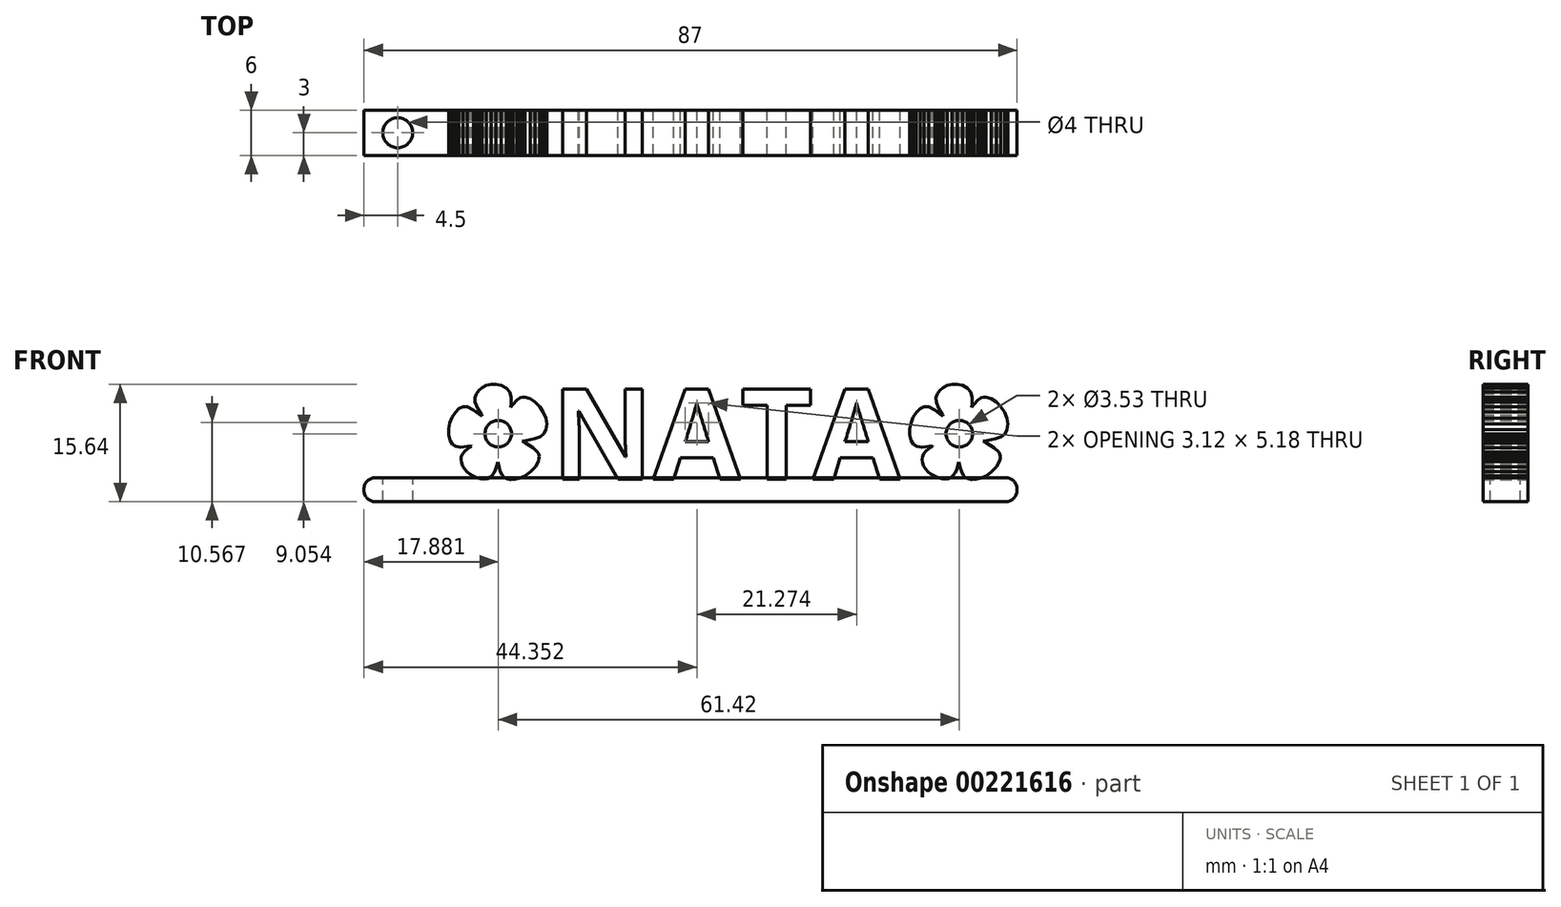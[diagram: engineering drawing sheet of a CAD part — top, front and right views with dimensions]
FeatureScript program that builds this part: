
annotation { "Feature Type Name" : "Feature", "Feature Type Description" : "" }
export const myFeature = defineFeature(function(context is Context, id is Id, definition is map)
    precondition{}
    {
        {
            var Q0;
            Q0=qCreatedBy(makeId("Front.planeOp"),FACE);
            var sketch = newSketch(context, id + "F0", { "sketchPlane" : qUnion([Q0])});
            skText(sketch, "E0", { "text": "    NATA", "fontName": "OpenSans-Bold.ttf"});
            skLineSegment(sketch, "E1.0.0", {"start": v(-9.3, 0.1) * mm, "end": v(-8.53, 0.46) * mm});
            skLineSegment(sketch, "E1.0.1", {"start": v(-8.53, 0.46) * mm, "end": v(-7.79, 1.02) * mm});
            skLineSegment(sketch, "E1.0.2", {"start": v(-7.79, 1.02) * mm, "end": v(-7.18, 1.67) * mm});
            skLineSegment(sketch, "E1.0.3", {"start": v(-7.18, 1.67) * mm, "end": v(-6.78, 2.35) * mm});
            skLineSegment(sketch, "E1.0.4", {"start": v(-6.78, 2.35) * mm, "end": v(-6.68, 2.7) * mm});
            skLineSegment(sketch, "E1.0.5", {"start": v(-6.68, 2.7) * mm, "end": v(-6.67, 3.02) * mm});
            skLineSegment(sketch, "E1.0.6", {"start": v(-6.67, 3.02) * mm, "end": v(-6.73, 3.33) * mm});
            skLineSegment(sketch, "E1.0.7", {"start": v(-6.73, 3.33) * mm, "end": v(-6.89, 3.62) * mm});
            skLineSegment(sketch, "E1.0.8", {"start": v(-6.89, 3.62) * mm, "end": v(-7.48, 4.2) * mm});
            skLineSegment(sketch, "E1.0.9", {"start": v(-7.48, 4.2) * mm, "end": v(-8.5, 4.79) * mm});
            skLineSegment(sketch, "E1.0.10", {"start": v(-8.5, 4.79) * mm, "end": v(-8.93, 5.06) * mm});
            skLineSegment(sketch, "E1.0.11", {"start": v(-8.93, 5.06) * mm, "end": v(-8.42, 5.16) * mm});
            skLineSegment(sketch, "E1.0.12", {"start": v(-8.42, 5.16) * mm, "end": v(-7.31, 5.37) * mm});
            skLineSegment(sketch, "E1.0.13", {"start": v(-7.31, 5.37) * mm, "end": v(-6.55, 5.65) * mm});
            skLineSegment(sketch, "E1.0.14", {"start": v(-6.55, 5.65) * mm, "end": v(-6.05, 6.04) * mm});
            skLineSegment(sketch, "E1.0.15", {"start": v(-6.05, 6.04) * mm, "end": v(-5.76, 6.58) * mm});
            skLineSegment(sketch, "E1.0.16", {"start": v(-5.76, 6.58) * mm, "end": v(-5.64, 7.33) * mm});
            skLineSegment(sketch, "E1.0.17", {"start": v(-5.64, 7.33) * mm, "end": v(-5.78, 8.14) * mm});
            skLineSegment(sketch, "E1.0.18", {"start": v(-5.78, 8.14) * mm, "end": v(-6.1, 8.93) * mm});
            skLineSegment(sketch, "E1.0.19", {"start": v(-6.1, 8.93) * mm, "end": v(-6.6, 9.67) * mm});
            skLineSegment(sketch, "E1.0.20", {"start": v(-6.6, 9.67) * mm, "end": v(-7.2, 10.28) * mm});
            skLineSegment(sketch, "E1.0.21", {"start": v(-7.2, 10.28) * mm, "end": v(-7.86, 10.72) * mm});
            skLineSegment(sketch, "E1.0.22", {"start": v(-7.86, 10.72) * mm, "end": v(-8.55, 10.93) * mm});
            skLineSegment(sketch, "E1.0.23", {"start": v(-8.55, 10.93) * mm, "end": v(-8.88, 10.93) * mm});
            skLineSegment(sketch, "E1.0.24", {"start": v(-8.88, 10.93) * mm, "end": v(-9.2, 10.85) * mm});
            skLineSegment(sketch, "E1.0.25", {"start": v(-9.2, 10.85) * mm, "end": v(-9.65, 10.56) * mm});
            skLineSegment(sketch, "E1.0.26", {"start": v(-9.65, 10.56) * mm, "end": v(-10.14, 9.98) * mm});
            skLineSegment(sketch, "E1.0.27", {"start": v(-10.14, 9.98) * mm, "end": v(-10.45, 9.58) * mm});
            skLineSegment(sketch, "E1.0.28", {"start": v(-10.45, 9.58) * mm, "end": v(-10.4, 10.03) * mm});
            skLineSegment(sketch, "E1.0.29", {"start": v(-10.4, 10.03) * mm, "end": v(-10.4, 10.93) * mm});
            skLineSegment(sketch, "E1.0.30", {"start": v(-10.4, 10.93) * mm, "end": v(-10.6, 11.63) * mm});
            skLineSegment(sketch, "E1.0.31", {"start": v(-10.6, 11.63) * mm, "end": v(-11.04, 12.15) * mm});
            skLineSegment(sketch, "E1.0.32", {"start": v(-11.04, 12.15) * mm, "end": v(-11.71, 12.5) * mm});
            skLineSegment(sketch, "E1.0.33", {"start": v(-11.71, 12.5) * mm, "end": v(-12.4, 12.64) * mm});
            skLineSegment(sketch, "E1.0.34", {"start": v(-12.4, 12.64) * mm, "end": v(-13.07, 12.62) * mm});
            skLineSegment(sketch, "E1.0.35", {"start": v(-13.07, 12.62) * mm, "end": v(-13.7, 12.47) * mm});
            skLineSegment(sketch, "E1.0.36", {"start": v(-13.7, 12.47) * mm, "end": v(-14.26, 12.2) * mm});
            skLineSegment(sketch, "E1.0.37", {"start": v(-14.26, 12.2) * mm, "end": v(-14.72, 11.83) * mm});
            skLineSegment(sketch, "E1.0.38", {"start": v(-14.72, 11.83) * mm, "end": v(-15.05, 11.38) * mm});
            skLineSegment(sketch, "E1.0.39", {"start": v(-15.05, 11.38) * mm, "end": v(-15.22, 10.87) * mm});
            skLineSegment(sketch, "E1.0.40", {"start": v(-15.22, 10.87) * mm, "end": v(-15.2, 10.3) * mm});
            skLineSegment(sketch, "E1.0.41", {"start": v(-15.2, 10.3) * mm, "end": v(-14.83, 9.4) * mm});
            skLineSegment(sketch, "E1.0.42", {"start": v(-14.83, 9.4) * mm, "end": v(-14.35, 8.55) * mm});
            skLineSegment(sketch, "E1.0.43", {"start": v(-14.35, 8.55) * mm, "end": v(-14.3, 8.4) * mm});
            skLineSegment(sketch, "E1.0.44", {"start": v(-14.3, 8.4) * mm, "end": v(-14.48, 8.53) * mm});
            skLineSegment(sketch, "E1.0.45", {"start": v(-14.48, 8.53) * mm, "end": v(-15.4, 9.23) * mm});
            skLineSegment(sketch, "E1.0.46", {"start": v(-15.4, 9.23) * mm, "end": v(-16.22, 9.63) * mm});
            skLineSegment(sketch, "E1.0.47", {"start": v(-16.22, 9.63) * mm, "end": v(-16.8, 9.63) * mm});
            skLineSegment(sketch, "E1.0.48", {"start": v(-16.8, 9.63) * mm, "end": v(-17.36, 9.37) * mm});
            skLineSegment(sketch, "E1.0.49", {"start": v(-17.36, 9.37) * mm, "end": v(-17.85, 8.9) * mm});
            skLineSegment(sketch, "E1.0.50", {"start": v(-17.85, 8.9) * mm, "end": v(-18.26, 8.26) * mm});
            skLineSegment(sketch, "E1.0.51", {"start": v(-18.26, 8.26) * mm, "end": v(-18.56, 7.51) * mm});
            skLineSegment(sketch, "E1.0.52", {"start": v(-18.56, 7.51) * mm, "end": v(-18.72, 6.71) * mm});
            skLineSegment(sketch, "E1.0.53", {"start": v(-18.72, 6.71) * mm, "end": v(-18.72, 5.9) * mm});
            skLineSegment(sketch, "E1.0.54", {"start": v(-18.72, 5.9) * mm, "end": v(-18.52, 5.16) * mm});
            skLineSegment(sketch, "E1.0.55", {"start": v(-18.52, 5.16) * mm, "end": v(-18.2, 4.64) * mm});
            skLineSegment(sketch, "E1.0.56", {"start": v(-18.2, 4.64) * mm, "end": v(-17.75, 4.36) * mm});
            skLineSegment(sketch, "E1.0.57", {"start": v(-17.75, 4.36) * mm, "end": v(-17.1, 4.27) * mm});
            skLineSegment(sketch, "E1.0.58", {"start": v(-17.1, 4.27) * mm, "end": v(-16.21, 4.37) * mm});
            skLineSegment(sketch, "E1.0.59", {"start": v(-16.21, 4.37) * mm, "end": v(-15.7, 4.43) * mm});
            skLineSegment(sketch, "E1.0.60", {"start": v(-15.7, 4.43) * mm, "end": v(-15.67, 4.4) * mm});
            skLineSegment(sketch, "E1.0.61", {"start": v(-15.67, 4.4) * mm, "end": v(-15.78, 4.33) * mm});
            skLineSegment(sketch, "E1.0.62", {"start": v(-15.78, 4.33) * mm, "end": v(-16.17, 4.07) * mm});
            skLineSegment(sketch, "E1.0.63", {"start": v(-16.17, 4.07) * mm, "end": v(-16.55, 3.71) * mm});
            skLineSegment(sketch, "E1.0.64", {"start": v(-16.55, 3.71) * mm, "end": v(-16.87, 3.33) * mm});
            skLineSegment(sketch, "E1.0.65", {"start": v(-16.87, 3.33) * mm, "end": v(-17.04, 3) * mm});
            skLineSegment(sketch, "E1.0.66", {"start": v(-17.04, 3) * mm, "end": v(-17.08, 2.6) * mm});
            skLineSegment(sketch, "E1.0.67", {"start": v(-17.08, 2.6) * mm, "end": v(-17.02, 2.2) * mm});
            skLineSegment(sketch, "E1.0.68", {"start": v(-17.02, 2.2) * mm, "end": v(-16.87, 1.78) * mm});
            skLineSegment(sketch, "E1.0.69", {"start": v(-16.87, 1.78) * mm, "end": v(-16.62, 1.39) * mm});
            skLineSegment(sketch, "E1.0.70", {"start": v(-16.62, 1.39) * mm, "end": v(-16.3, 1.02) * mm});
            skLineSegment(sketch, "E1.0.71", {"start": v(-16.3, 1.02) * mm, "end": v(-15.9, 0.69) * mm});
            skLineSegment(sketch, "E1.0.72", {"start": v(-15.9, 0.69) * mm, "end": v(-15.45, 0.4) * mm});
            skLineSegment(sketch, "E1.0.73", {"start": v(-15.45, 0.4) * mm, "end": v(-14.95, 0.2) * mm});
            skLineSegment(sketch, "E1.0.74", {"start": v(-14.95, 0.2) * mm, "end": v(-14.44, 0.06) * mm});
            skLineSegment(sketch, "E1.0.75", {"start": v(-14.44, 0.06) * mm, "end": v(-13.98, 0.02) * mm});
            skLineSegment(sketch, "E1.0.76", {"start": v(-13.98, 0.02) * mm, "end": v(-13.58, 0.08) * mm});
            skLineSegment(sketch, "E1.0.77", {"start": v(-13.58, 0.08) * mm, "end": v(-13.23, 0.23) * mm});
            skLineSegment(sketch, "E1.0.78", {"start": v(-13.23, 0.23) * mm, "end": v(-12.92, 0.49) * mm});
            skLineSegment(sketch, "E1.0.79", {"start": v(-12.92, 0.49) * mm, "end": v(-12.67, 0.84) * mm});
            skLineSegment(sketch, "E1.0.80", {"start": v(-12.67, 0.84) * mm, "end": v(-12.46, 1.28) * mm});
            skLineSegment(sketch, "E1.0.81", {"start": v(-12.46, 1.28) * mm, "end": v(-12.3, 1.83) * mm});
            skLineSegment(sketch, "E1.0.82", {"start": v(-12.3, 1.83) * mm, "end": v(-12.19, 2.26) * mm});
            skLineSegment(sketch, "E1.0.83", {"start": v(-12.19, 2.26) * mm, "end": v(-12.13, 2.1) * mm});
            skLineSegment(sketch, "E1.0.84", {"start": v(-12.13, 2.1) * mm, "end": v(-12.01, 1.53) * mm});
            skLineSegment(sketch, "E1.0.85", {"start": v(-12.01, 1.53) * mm, "end": v(-11.82, 1) * mm});
            skLineSegment(sketch, "E1.0.86", {"start": v(-11.82, 1) * mm, "end": v(-11.6, 0.55) * mm});
            skLineSegment(sketch, "E1.0.87", {"start": v(-11.6, 0.55) * mm, "end": v(-11.35, 0.26) * mm});
            skLineSegment(sketch, "E1.0.88", {"start": v(-11.35, 0.26) * mm, "end": v(-10.95, 0.05) * mm});
            skLineSegment(sketch, "E1.0.89", {"start": v(-10.95, 0.05) * mm, "end": v(-10.46, -0.04) * mm});
            skLineSegment(sketch, "E1.0.90", {"start": v(-10.46, -0.04) * mm, "end": v(-9.9, -0.03) * mm});
            skLineSegment(sketch, "E1.0.91", {"start": v(-9.9, -0.03) * mm, "end": v(-9.3, 0.1) * mm});
            skCircle(sketch, "E2", {"center": v(-12.12, 6.05) * mm, "radius": 1.77 * mm});
            skCircle(sketch, "E3.1.0.0", {"center": v(49.3, 6.05) * mm, "radius": 1.77 * mm});
            skLineSegment(sketch, "E3.1.0.1", {"start": v(50.97, 9.58) * mm, "end": v(51.01, 10.03) * mm});
            skLineSegment(sketch, "E3.1.0.2", {"start": v(54.22, 10.28) * mm, "end": v(53.56, 10.72) * mm});
            skLineSegment(sketch, "E3.1.0.3", {"start": v(42.7, 5.9) * mm, "end": v(42.9, 5.16) * mm});
            skLineSegment(sketch, "E3.1.0.4", {"start": v(47.16, 12.2) * mm, "end": v(46.7, 11.83) * mm});
            skLineSegment(sketch, "E3.1.0.5", {"start": v(45.12, 1.02) * mm, "end": v(45.51, 0.69) * mm});
            skLineSegment(sketch, "E3.1.0.6", {"start": v(45.2, 9.63) * mm, "end": v(44.62, 9.63) * mm});
            skLineSegment(sketch, "E3.1.0.7", {"start": v(42.86, 7.51) * mm, "end": v(42.7, 6.71) * mm});
            skLineSegment(sketch, "E3.1.0.8", {"start": v(46.03, 9.23) * mm, "end": v(45.2, 9.63) * mm});
            skLineSegment(sketch, "E3.1.0.9", {"start": v(44.62, 9.63) * mm, "end": v(44.06, 9.37) * mm});
            skLineSegment(sketch, "E3.1.0.10", {"start": v(51.28, 9.98) * mm, "end": v(50.97, 9.58) * mm});
            skLineSegment(sketch, "E3.1.0.11", {"start": v(50.82, 11.63) * mm, "end": v(50.38, 12.15) * mm});
            skLineSegment(sketch, "E3.1.0.12", {"start": v(50.38, 12.15) * mm, "end": v(49.7, 12.5) * mm});
            skLineSegment(sketch, "E3.1.0.13", {"start": v(51.03, 10.93) * mm, "end": v(50.82, 11.63) * mm});
            skLineSegment(sketch, "E3.1.0.14", {"start": v(45.97, 0.4) * mm, "end": v(46.47, 0.2) * mm});
            skLineSegment(sketch, "E3.1.0.15", {"start": v(51.52, -0.03) * mm, "end": v(52.11, 0.1) * mm});
            skLineSegment(sketch, "E3.1.0.16", {"start": v(42.7, 6.71) * mm, "end": v(42.7, 5.9) * mm});
            skLineSegment(sketch, "E3.1.0.17", {"start": v(52.11, 0.1) * mm, "end": v(52.89, 0.46) * mm});
            skLineSegment(sketch, "E3.1.0.18", {"start": v(45.51, 0.69) * mm, "end": v(45.97, 0.4) * mm});
            skLineSegment(sketch, "E3.1.0.19", {"start": v(42.9, 5.16) * mm, "end": v(43.22, 4.64) * mm});
            skLineSegment(sketch, "E3.1.0.20", {"start": v(54.1, 5.37) * mm, "end": v(54.87, 5.65) * mm});
            skLineSegment(sketch, "E3.1.0.21", {"start": v(52.89, 0.46) * mm, "end": v(53.63, 1.02) * mm});
            skLineSegment(sketch, "E3.1.0.22", {"start": v(54.82, 9.67) * mm, "end": v(54.22, 10.28) * mm});
            skLineSegment(sketch, "E3.1.0.23", {"start": v(51.01, 10.03) * mm, "end": v(51.03, 10.93) * mm});
            skLineSegment(sketch, "E3.1.0.24", {"start": v(44.06, 9.37) * mm, "end": v(43.57, 8.9) * mm});
            skLineSegment(sketch, "E3.1.0.25", {"start": v(49.7, 12.5) * mm, "end": v(49.02, 12.64) * mm});
            skLineSegment(sketch, "E3.1.0.26", {"start": v(48.35, 12.62) * mm, "end": v(47.72, 12.47) * mm});
            skLineSegment(sketch, "E3.1.0.27", {"start": v(54.24, 1.67) * mm, "end": v(54.64, 2.35) * mm});
            skLineSegment(sketch, "E3.1.0.28", {"start": v(55.31, 8.93) * mm, "end": v(54.82, 9.67) * mm});
            skLineSegment(sketch, "E3.1.0.29", {"start": v(49.02, 12.64) * mm, "end": v(48.35, 12.62) * mm});
            skLineSegment(sketch, "E3.1.0.30", {"start": v(53.63, 1.02) * mm, "end": v(54.24, 1.67) * mm});
            skLineSegment(sketch, "E3.1.0.31", {"start": v(43.57, 8.9) * mm, "end": v(43.16, 8.26) * mm});
            skLineSegment(sketch, "E3.1.0.32", {"start": v(43.16, 8.26) * mm, "end": v(42.86, 7.51) * mm});
            skLineSegment(sketch, "E3.1.0.33", {"start": v(47.72, 12.47) * mm, "end": v(47.16, 12.2) * mm});
            skLineSegment(sketch, "E3.1.0.34", {"start": v(54.64, 2.35) * mm, "end": v(54.74, 2.7) * mm});
            skLineSegment(sketch, "E3.1.0.35", {"start": v(44.62, 9.63) * mm, "end": v(44.06, 9.37) * mm});
            skLineSegment(sketch, "E3.1.0.36", {"start": v(49.02, 12.64) * mm, "end": v(48.35, 12.62) * mm});
            skLineSegment(sketch, "E3.1.0.37", {"start": v(54.1, 5.37) * mm, "end": v(54.87, 5.65) * mm});
            skLineSegment(sketch, "E3.1.0.38", {"start": v(50.47, 0.05) * mm, "end": v(50.97, -0.04) * mm});
            skLineSegment(sketch, "E3.1.0.39", {"start": v(55.31, 8.93) * mm, "end": v(54.82, 9.67) * mm});
            skLineSegment(sketch, "E3.1.0.40", {"start": v(51.52, -0.03) * mm, "end": v(52.11, 0.1) * mm});
            skLineSegment(sketch, "E3.1.0.41", {"start": v(51.28, 9.98) * mm, "end": v(50.97, 9.58) * mm});
            skLineSegment(sketch, "E3.1.0.42", {"start": v(53.63, 1.02) * mm, "end": v(54.24, 1.67) * mm});
            skLineSegment(sketch, "E3.1.0.43", {"start": v(54.64, 2.35) * mm, "end": v(54.74, 2.7) * mm});
            skLineSegment(sketch, "E3.1.0.44", {"start": v(42.7, 6.71) * mm, "end": v(42.7, 5.9) * mm});
            skLineSegment(sketch, "E3.1.0.45", {"start": v(52.11, 0.1) * mm, "end": v(52.89, 0.46) * mm});
            skLineSegment(sketch, "E3.1.0.46", {"start": v(48.35, 12.62) * mm, "end": v(47.72, 12.47) * mm});
            skLineSegment(sketch, "E3.1.0.47", {"start": v(47.16, 12.2) * mm, "end": v(46.7, 11.83) * mm});
            skLineSegment(sketch, "E3.1.0.48", {"start": v(45.97, 0.4) * mm, "end": v(46.47, 0.2) * mm});
            skLineSegment(sketch, "E3.1.0.49", {"start": v(51.01, 10.03) * mm, "end": v(51.03, 10.93) * mm});
            skLineSegment(sketch, "E3.1.0.50", {"start": v(50.97, 9.58) * mm, "end": v(51.01, 10.03) * mm});
            skLineSegment(sketch, "E3.1.0.51", {"start": v(50.97, -0.04) * mm, "end": v(51.52, -0.03) * mm});
            skLineSegment(sketch, "E3.1.0.52", {"start": v(45.2, 9.63) * mm, "end": v(44.62, 9.63) * mm});
            skLineSegment(sketch, "E3.1.0.53", {"start": v(51.03, 10.93) * mm, "end": v(50.82, 11.63) * mm});
            skLineSegment(sketch, "E3.1.0.54", {"start": v(54.22, 10.28) * mm, "end": v(53.56, 10.72) * mm});
            skLineSegment(sketch, "E3.1.0.55", {"start": v(43.57, 8.9) * mm, "end": v(43.16, 8.26) * mm});
            skLineSegment(sketch, "E3.1.0.56", {"start": v(45.51, 0.69) * mm, "end": v(45.97, 0.4) * mm});
            skLineSegment(sketch, "E3.1.0.57", {"start": v(49.7, 12.5) * mm, "end": v(49.02, 12.64) * mm});
            skLineSegment(sketch, "E3.1.0.58", {"start": v(44.06, 9.37) * mm, "end": v(43.57, 8.9) * mm});
            skLineSegment(sketch, "E3.1.0.59", {"start": v(42.7, 5.9) * mm, "end": v(42.9, 5.16) * mm});
            skLineSegment(sketch, "E3.1.0.60", {"start": v(50.38, 12.15) * mm, "end": v(49.7, 12.5) * mm});
            skLineSegment(sketch, "E3.1.0.61", {"start": v(46.03, 9.23) * mm, "end": v(45.2, 9.63) * mm});
            skLineSegment(sketch, "E3.1.0.62", {"start": v(52.89, 0.46) * mm, "end": v(53.63, 1.02) * mm});
            skLineSegment(sketch, "E3.1.0.63", {"start": v(50.82, 11.63) * mm, "end": v(50.38, 12.15) * mm});
            skLineSegment(sketch, "E3.1.0.64", {"start": v(43.16, 8.26) * mm, "end": v(42.86, 7.51) * mm});
            skLineSegment(sketch, "E3.1.0.65", {"start": v(54.24, 1.67) * mm, "end": v(54.64, 2.35) * mm});
            skLineSegment(sketch, "E3.1.0.66", {"start": v(42.86, 7.51) * mm, "end": v(42.7, 6.71) * mm});
            skLineSegment(sketch, "E3.1.0.67", {"start": v(45.12, 1.02) * mm, "end": v(45.51, 0.69) * mm});
            skLineSegment(sketch, "E3.1.0.68", {"start": v(42.9, 5.16) * mm, "end": v(43.22, 4.64) * mm});
            skLineSegment(sketch, "E3.1.0.69", {"start": v(47.72, 12.47) * mm, "end": v(47.16, 12.2) * mm});
            skLineSegment(sketch, "E3.1.0.70", {"start": v(54.82, 9.67) * mm, "end": v(54.22, 10.28) * mm});
            skLineSegment(sketch, "E3.1.0.71", {"start": v(46.7, 11.83) * mm, "end": v(46.37, 11.38) * mm});
            skLineSegment(sketch, "E3.1.0.72", {"start": v(53.56, 10.72) * mm, "end": v(52.87, 10.93) * mm});
            skLineSegment(sketch, "E3.1.0.73", {"start": v(55.37, 6.04) * mm, "end": v(55.67, 6.58) * mm});
            skLineSegment(sketch, "E3.1.0.74", {"start": v(54.74, 2.7) * mm, "end": v(54.76, 3.02) * mm});
            skLineSegment(sketch, "E3.1.0.75", {"start": v(52.87, 10.93) * mm, "end": v(52.54, 10.93) * mm});
            skLineSegment(sketch, "E3.1.0.76", {"start": v(43.22, 4.64) * mm, "end": v(43.67, 4.36) * mm});
            skLineSegment(sketch, "E3.1.0.77", {"start": v(52.22, 10.85) * mm, "end": v(51.77, 10.56) * mm});
            skLineSegment(sketch, "E3.1.0.78", {"start": v(53, 5.16) * mm, "end": v(54.1, 5.37) * mm});
            skLineSegment(sketch, "E3.1.0.79", {"start": v(54.76, 3.02) * mm, "end": v(54.69, 3.33) * mm});
            skLineSegment(sketch, "E3.1.0.80", {"start": v(54.69, 3.33) * mm, "end": v(54.53, 3.62) * mm});
            skLineSegment(sketch, "E3.1.0.81", {"start": v(53.94, 4.2) * mm, "end": v(52.93, 4.79) * mm});
            skLineSegment(sketch, "E3.1.0.82", {"start": v(55.78, 7.33) * mm, "end": v(55.65, 8.14) * mm});
            skLineSegment(sketch, "E3.1.0.83", {"start": v(44.8, 1.39) * mm, "end": v(45.12, 1.02) * mm});
            skLineSegment(sketch, "E3.1.0.84", {"start": v(46.98, 0.06) * mm, "end": v(47.44, 0.02) * mm});
            skLineSegment(sketch, "E3.1.0.85", {"start": v(52.5, 5.06) * mm, "end": v(53, 5.16) * mm});
            skLineSegment(sketch, "E3.1.0.86", {"start": v(50.07, 0.26) * mm, "end": v(50.47, 0.05) * mm});
            skLineSegment(sketch, "E3.1.0.87", {"start": v(46.37, 11.38) * mm, "end": v(46.2, 10.87) * mm});
            skLineSegment(sketch, "E3.1.0.88", {"start": v(55.67, 6.58) * mm, "end": v(55.78, 7.33) * mm});
            skLineSegment(sketch, "E3.1.0.89", {"start": v(50.47, 0.05) * mm, "end": v(50.97, -0.04) * mm});
            skLineSegment(sketch, "E3.1.0.90", {"start": v(52.93, 4.79) * mm, "end": v(52.5, 5.06) * mm});
            skLineSegment(sketch, "E3.1.0.91", {"start": v(46.47, 0.2) * mm, "end": v(46.98, 0.06) * mm});
            skLineSegment(sketch, "E3.1.0.92", {"start": v(46.22, 10.3) * mm, "end": v(46.6, 9.4) * mm});
            skLineSegment(sketch, "E3.1.0.93", {"start": v(44.55, 1.78) * mm, "end": v(44.8, 1.39) * mm});
            skLineSegment(sketch, "E3.1.0.94", {"start": v(54.53, 3.62) * mm, "end": v(53.94, 4.2) * mm});
            skLineSegment(sketch, "E3.1.0.95", {"start": v(50.97, -0.04) * mm, "end": v(51.52, -0.03) * mm});
            skLineSegment(sketch, "E3.1.0.96", {"start": v(46.2, 10.87) * mm, "end": v(46.22, 10.3) * mm});
            skLineSegment(sketch, "E3.1.0.97", {"start": v(54.87, 5.65) * mm, "end": v(55.37, 6.04) * mm});
            skLineSegment(sketch, "E3.1.0.98", {"start": v(52.54, 10.93) * mm, "end": v(52.22, 10.85) * mm});
            skLineSegment(sketch, "E3.1.0.99", {"start": v(51.77, 10.56) * mm, "end": v(51.28, 9.98) * mm});
            skLineSegment(sketch, "E3.1.0.100", {"start": v(47.44, 0.02) * mm, "end": v(47.84, 0.08) * mm});
            skLineSegment(sketch, "E3.1.0.101", {"start": v(44.4, 2.2) * mm, "end": v(44.55, 1.78) * mm});
            skLineSegment(sketch, "E3.1.0.102", {"start": v(55.65, 8.14) * mm, "end": v(55.31, 8.93) * mm});
            skLineSegment(sketch, "E3.1.0.103", {"start": v(52.93, 4.79) * mm, "end": v(52.5, 5.06) * mm});
            skLineSegment(sketch, "E3.1.0.104", {"start": v(52.5, 5.06) * mm, "end": v(53, 5.16) * mm});
            skLineSegment(sketch, "E3.1.0.105", {"start": v(43.22, 4.64) * mm, "end": v(43.67, 4.36) * mm});
            skLineSegment(sketch, "E3.1.0.106", {"start": v(49.82, 0.55) * mm, "end": v(50.07, 0.26) * mm});
            skLineSegment(sketch, "E3.1.0.107", {"start": v(50.07, 0.26) * mm, "end": v(50.47, 0.05) * mm});
            skLineSegment(sketch, "E3.1.0.108", {"start": v(44.55, 1.78) * mm, "end": v(44.8, 1.39) * mm});
            skLineSegment(sketch, "E3.1.0.109", {"start": v(54.53, 3.62) * mm, "end": v(53.94, 4.2) * mm});
            skLineSegment(sketch, "E3.1.0.110", {"start": v(53, 5.16) * mm, "end": v(54.1, 5.37) * mm});
            skLineSegment(sketch, "E3.1.0.111", {"start": v(46.22, 10.3) * mm, "end": v(46.6, 9.4) * mm});
            skLineSegment(sketch, "E3.1.0.112", {"start": v(54.87, 5.65) * mm, "end": v(55.37, 6.04) * mm});
            skLineSegment(sketch, "E3.1.0.113", {"start": v(51.77, 10.56) * mm, "end": v(51.28, 9.98) * mm});
            skLineSegment(sketch, "E3.1.0.114", {"start": v(55.67, 6.58) * mm, "end": v(55.78, 7.33) * mm});
            skLineSegment(sketch, "E3.1.0.115", {"start": v(46.2, 10.87) * mm, "end": v(46.22, 10.3) * mm});
            skLineSegment(sketch, "E3.1.0.116", {"start": v(52.54, 10.93) * mm, "end": v(52.22, 10.85) * mm});
            skLineSegment(sketch, "E3.1.0.117", {"start": v(47.44, 0.02) * mm, "end": v(47.84, 0.08) * mm});
            skLineSegment(sketch, "E3.1.0.118", {"start": v(52.22, 10.85) * mm, "end": v(51.77, 10.56) * mm});
            skLineSegment(sketch, "E3.1.0.119", {"start": v(46.98, 0.06) * mm, "end": v(47.44, 0.02) * mm});
            skLineSegment(sketch, "E3.1.0.120", {"start": v(46.47, 0.2) * mm, "end": v(46.98, 0.06) * mm});
            skLineSegment(sketch, "E3.1.0.121", {"start": v(53.94, 4.2) * mm, "end": v(52.93, 4.79) * mm});
            skLineSegment(sketch, "E3.1.0.122", {"start": v(55.37, 6.04) * mm, "end": v(55.67, 6.58) * mm});
            skLineSegment(sketch, "E3.1.0.123", {"start": v(44.34, 2.6) * mm, "end": v(44.4, 2.2) * mm});
            skLineSegment(sketch, "E3.1.0.124", {"start": v(54.74, 2.7) * mm, "end": v(54.76, 3.02) * mm});
            skLineSegment(sketch, "E3.1.0.125", {"start": v(44.8, 1.39) * mm, "end": v(45.12, 1.02) * mm});
            skLineSegment(sketch, "E3.1.0.126", {"start": v(55.65, 8.14) * mm, "end": v(55.31, 8.93) * mm});
            skLineSegment(sketch, "E3.1.0.127", {"start": v(55.78, 7.33) * mm, "end": v(55.65, 8.14) * mm});
            skLineSegment(sketch, "E3.1.0.128", {"start": v(54.76, 3.02) * mm, "end": v(54.69, 3.33) * mm});
            skLineSegment(sketch, "E3.1.0.129", {"start": v(44.4, 2.2) * mm, "end": v(44.55, 1.78) * mm});
            skLineSegment(sketch, "E3.1.0.130", {"start": v(54.69, 3.33) * mm, "end": v(54.53, 3.62) * mm});
            skLineSegment(sketch, "E3.1.0.131", {"start": v(46.37, 11.38) * mm, "end": v(46.2, 10.87) * mm});
            skLineSegment(sketch, "E3.1.0.132", {"start": v(52.87, 10.93) * mm, "end": v(52.54, 10.93) * mm});
            skLineSegment(sketch, "E3.1.0.133", {"start": v(53.56, 10.72) * mm, "end": v(52.87, 10.93) * mm});
            skLineSegment(sketch, "E3.1.0.134", {"start": v(46.7, 11.83) * mm, "end": v(46.37, 11.38) * mm});
            skLineSegment(sketch, "E3.1.0.135", {"start": v(44.34, 2.6) * mm, "end": v(44.4, 2.2) * mm});
            skLineSegment(sketch, "E3.1.0.136", {"start": v(45.2, 4.37) * mm, "end": v(45.72, 4.43) * mm});
            skLineSegment(sketch, "E3.1.0.137", {"start": v(49.4, 1.53) * mm, "end": v(49.6, 1) * mm});
            skLineSegment(sketch, "E3.1.0.138", {"start": v(45.64, 4.33) * mm, "end": v(45.26, 4.07) * mm});
            skLineSegment(sketch, "E3.1.0.139", {"start": v(48.2, 0.23) * mm, "end": v(48.5, 0.49) * mm});
            skLineSegment(sketch, "E3.1.0.140", {"start": v(48.75, 0.84) * mm, "end": v(48.96, 1.28) * mm});
            skLineSegment(sketch, "E3.1.0.141", {"start": v(49.6, 1) * mm, "end": v(49.82, 0.55) * mm});
            skLineSegment(sketch, "E3.1.0.142", {"start": v(45.26, 4.07) * mm, "end": v(44.87, 3.71) * mm});
            skLineSegment(sketch, "E3.1.0.143", {"start": v(49.29, 2.1) * mm, "end": v(49.4, 1.53) * mm});
            skLineSegment(sketch, "E3.1.0.144", {"start": v(48.5, 0.49) * mm, "end": v(48.75, 0.84) * mm});
            skLineSegment(sketch, "E3.1.0.145", {"start": v(44.31, 4.27) * mm, "end": v(45.2, 4.37) * mm});
            skLineSegment(sketch, "E3.1.0.146", {"start": v(44.87, 3.71) * mm, "end": v(44.55, 3.33) * mm});
            skLineSegment(sketch, "E3.1.0.147", {"start": v(43.67, 4.36) * mm, "end": v(44.31, 4.27) * mm});
            skLineSegment(sketch, "E3.1.0.148", {"start": v(48.96, 1.28) * mm, "end": v(49.12, 1.83) * mm});
            skLineSegment(sketch, "E3.1.0.149", {"start": v(49.23, 2.26) * mm, "end": v(49.29, 2.1) * mm});
            skLineSegment(sketch, "E3.1.0.150", {"start": v(44.55, 3.33) * mm, "end": v(44.38, 3) * mm});
            skLineSegment(sketch, "E3.1.0.151", {"start": v(49.82, 0.55) * mm, "end": v(50.07, 0.26) * mm});
            skLineSegment(sketch, "E3.1.0.152", {"start": v(49.12, 1.83) * mm, "end": v(49.23, 2.26) * mm});
            skLineSegment(sketch, "E3.1.0.153", {"start": v(44.38, 3) * mm, "end": v(44.34, 2.6) * mm});
            skLineSegment(sketch, "E3.1.0.154", {"start": v(47.84, 0.08) * mm, "end": v(48.2, 0.23) * mm});
            skLineSegment(sketch, "E3.1.0.155", {"start": v(45.75, 4.4) * mm, "end": v(45.64, 4.33) * mm});
            skLineSegment(sketch, "E3.1.0.156", {"start": v(49.23, 2.26) * mm, "end": v(49.29, 2.1) * mm});
            skLineSegment(sketch, "E3.1.0.157", {"start": v(44.31, 4.27) * mm, "end": v(45.2, 4.37) * mm});
            skLineSegment(sketch, "E3.1.0.158", {"start": v(49.4, 1.53) * mm, "end": v(49.6, 1) * mm});
            skLineSegment(sketch, "E3.1.0.159", {"start": v(45.72, 4.43) * mm, "end": v(45.75, 4.4) * mm});
            skLineSegment(sketch, "E3.1.0.160", {"start": v(44.87, 3.71) * mm, "end": v(44.55, 3.33) * mm});
            skLineSegment(sketch, "E3.1.0.161", {"start": v(43.67, 4.36) * mm, "end": v(44.31, 4.27) * mm});
            skLineSegment(sketch, "E3.1.0.162", {"start": v(45.2, 4.37) * mm, "end": v(45.72, 4.43) * mm});
            skLineSegment(sketch, "E3.1.0.163", {"start": v(47.84, 0.08) * mm, "end": v(48.2, 0.23) * mm});
            skLineSegment(sketch, "E3.1.0.164", {"start": v(45.26, 4.07) * mm, "end": v(44.87, 3.71) * mm});
            skLineSegment(sketch, "E3.1.0.165", {"start": v(49.29, 2.1) * mm, "end": v(49.4, 1.53) * mm});
            skLineSegment(sketch, "E3.1.0.166", {"start": v(49.12, 1.83) * mm, "end": v(49.23, 2.26) * mm});
            skLineSegment(sketch, "E3.1.0.167", {"start": v(45.64, 4.33) * mm, "end": v(45.26, 4.07) * mm});
            skLineSegment(sketch, "E3.1.0.168", {"start": v(48.2, 0.23) * mm, "end": v(48.5, 0.49) * mm});
            skLineSegment(sketch, "E3.1.0.169", {"start": v(44.38, 3) * mm, "end": v(44.34, 2.6) * mm});
            skLineSegment(sketch, "E3.1.0.170", {"start": v(49.6, 1) * mm, "end": v(49.82, 0.55) * mm});
            skLineSegment(sketch, "E3.1.0.171", {"start": v(48.5, 0.49) * mm, "end": v(48.75, 0.84) * mm});
            skLineSegment(sketch, "E3.1.0.172", {"start": v(48.75, 0.84) * mm, "end": v(48.96, 1.28) * mm});
            skLineSegment(sketch, "E3.1.0.173", {"start": v(44.55, 3.33) * mm, "end": v(44.38, 3) * mm});
            skLineSegment(sketch, "E3.1.0.174", {"start": v(48.96, 1.28) * mm, "end": v(49.12, 1.83) * mm});
            skLineSegment(sketch, "E3.1.0.175", {"start": v(45.75, 4.4) * mm, "end": v(45.64, 4.33) * mm});
            skLineSegment(sketch, "E3.1.0.176", {"start": v(45.72, 4.43) * mm, "end": v(45.75, 4.4) * mm});
            skLineSegment(sketch, "E3.1.0.177", {"start": v(47.13, 8.4) * mm, "end": v(46.94, 8.53) * mm});
            skLineSegment(sketch, "E3.1.0.178", {"start": v(47.07, 8.55) * mm, "end": v(47.13, 8.4) * mm});
            skLineSegment(sketch, "E3.1.0.179", {"start": v(46.6, 9.4) * mm, "end": v(47.07, 8.55) * mm});
            skLineSegment(sketch, "E3.1.0.180", {"start": v(46.94, 8.53) * mm, "end": v(46.03, 9.23) * mm});
            skLineSegment(sketch, "E3.1.0.181", {"start": v(47.07, 8.55) * mm, "end": v(47.13, 8.4) * mm});
            skLineSegment(sketch, "E3.1.0.182", {"start": v(46.6, 9.4) * mm, "end": v(47.07, 8.55) * mm});
            skLineSegment(sketch, "E3.1.0.183", {"start": v(46.94, 8.53) * mm, "end": v(46.03, 9.23) * mm});
            skLineSegment(sketch, "E3.1.0.184", {"start": v(47.13, 8.4) * mm, "end": v(46.94, 8.53) * mm});
            skLineSegment(sketch, "E3.direction1", {"start": v(-16.3, 1.02) * mm, "end": v(42.4, 1.02) * mm, "construction": true});
            const initialGuessF0  = {"E0": [-0.0225, 0, 1, 0, 0.01207]};
            skSetInitialGuess(sketch, initialGuessF0);
            skSolve(sketch);
        }
        {
            var Q0;
            Q0=qSketchRegion(id+"F0",true);
            extrude(context, id + "F1", {"entities" : qUnion([Q0]), "endBound" : BoundingType.SYMMETRIC, "depth" : 6 * mm});
        }
        {
            var Q0;
            Q0=qCreatedBy(makeId("Top.planeOp"),FACE);
            var sketch = newSketch(context, id + "F2", { "sketchPlane" : qUnion([Q0])});
            skLineSegment(sketch, "E4.bottom", {"start": v(-22.5, 3) * mm, "end": v(57, 3) * mm});
            skLineSegment(sketch, "E4.top", {"start": v(-22.5, -3) * mm, "end": v(57, -3) * mm});
            skLineSegment(sketch, "E4.left", {"start": v(-22.5, 3) * mm, "end": v(-22.5, -3) * mm});
            skLineSegment(sketch, "E4.right", {"start": v(57, 3) * mm, "end": v(57, -3) * mm});
            skSolve(sketch);
        }
        {
            var Q0;
            Q0=makeQuery(id+"F2.imprint","IMPRINT",FACE,{"disambiguationData":[TD([[makeQuery(id+"F2.imprint","IMPRINT",EDGE,{"derivedFrom":sQuery(id+"F2.wireOp",EDGE,"E4.bottom")}),-1.0]])]});
            extrude(context, id + "F3", {"entities" : qUnion([Q0]), "depth" : 0.2 * mm});
        }
        {
            var Q0;
            Q0=makeQuery(id+"F3.opExtrude","CAP_FACE",FACE,{"disambiguationData":[OSD([sQuery(id+"F2.wireOp",EDGE,"E4.bottom"),sQuery(id+"F2.wireOp",EDGE,"E4.top"),sQuery(id+"F2.wireOp",EDGE,"E4.left"),sQuery(id+"F2.wireOp",EDGE,"E4.right")])],"isStart":true});
            extrude(context, id + "F4", {"entities" : qUnion([Q0]), "depth" : 3 * mm});
        }
        {
            var Q0;
            {var subQ0=sQuery(id+"F2.wireOp",EDGE,"E4.left");Q0=makeQuery(id+"FaVoHrOpcFZXiYX_6.opBoolean","MERGE",FACE,{"derivedFrom":[makeQuery(id+"F3.opExtrude","SWEPT_FACE",FACE,{"disambiguationData":[OSD([subQ0])]}),makeQuery(id+"F4.opExtrude","SWEPT_FACE",FACE,{"disambiguationData":[OSD([subQ0])]})]});}
            var sketch = newSketch(context, id + "F5", { "sketchPlane" : qUnion([Q0])});
            skLineSegment(sketch, "E5.bottom", {"start": v(-3, -3) * mm, "end": v(3, -3) * mm});
            skLineSegment(sketch, "E5.top", {"start": v(-3, 0.2) * mm, "end": v(3, 0.2) * mm});
            skLineSegment(sketch, "E5.left", {"start": v(-3, -3) * mm, "end": v(-3, 0.2) * mm});
            skLineSegment(sketch, "E5.right", {"start": v(3, -3) * mm, "end": v(3, 0.2) * mm});
            skSolve(sketch);
        }
        {
            var Q0;
            Q0=qSketchRegion(id+"F5",true);
            extrude(context, id + "F6", {"entities" : qUnion([Q0]), "operationType" : NewBodyOperationType.ADD, "depth" : 7.5 * mm});
        }
        {
            var Q0;
            Q0=makeQuery(id+"F6.opExtrude","CAP_EDGE",EDGE,{"disambiguationData":[OSD([sQuery(id+"F5.wireOp",EDGE,"E5.bottom")])],"isStart":false});
            var Q1;
            Q1=makeQuery(id+"F6.opExtrude","CAP_EDGE",EDGE,{"disambiguationData":[OSD([sQuery(id+"F5.wireOp",EDGE,"E5.top")])],"isStart":false});
            var Q2;
            Q2=makeQuery(id+"F4.opExtrude","CAP_EDGE",EDGE,{"disambiguationData":[OSD([sQuery(id+"F2.wireOp",EDGE,"E4.right")])],"isStart":false});
            fillet(context, id + "F7", {"entities" : qUnion([Q0, Q1, Q2]), "radius" : 1.5 * mm, "tangentPropagation" : true, "allowEdgeOverflow" : false});
        }
        {
            var Q0;
            {var subQ19=sQuery(id+"F2.wireOp",EDGE,"E4.top");var subQ20=sQuery(id+"F2.wireOp",EDGE,"E4.bottom");var subQ63=sQuery(id+"F0.wireOp",EDGE,"E0.sketch_text.stroke-2");var subQ66=sQuery(id+"F2.wireOp",EDGE,"E4.left");Q0=makeQuery(id+"F6.boolean.opBoolean","MERGE",FACE,{"derivedFrom":[makeQuery(id+"FaVoHrOpcFZXiYX_6.opBoolean","SPLIT",FACE,{"disambiguationData":[TD([makeQuery(id+"F1.opExtrude","SWEPT_FACE",FACE,{"disambiguationData":[OSD([subQ63])]})])],"derivedFrom":makeQuery(id+"F3.opExtrude","CAP_FACE",FACE,{"disambiguationData":[OSD([subQ20,subQ19,subQ66,sQuery(id+"F2.wireOp",EDGE,"E4.right")])],"isStart":false})}),makeQuery(id+"F6.opExtrude","SWEPT_FACE",FACE,{"disambiguationData":[OSD([sQuery(id+"F5.wireOp",EDGE,"E5.top")])]})]});}
            var sketch = newSketch(context, id + "F8", { "sketchPlane" : qUnion([Q0])});
            skCircle(sketch, "E6", {"center": v(-25.5, 0) * mm, "radius": 2 * mm});
            skSolve(sketch);
        }
        {
            var Q0;
            Q0=makeQuery(id+"F8.imprint","IMPRINT",FACE,{"disambiguationData":[TD([[makeQuery(id+"F8.imprint","IMPRINT",EDGE,{"derivedFrom":sQuery(id+"F8.wireOp",EDGE,"E6")}),1.0]])]});
            extrude(context, id + "F9", {"entities" : qUnion([Q0]), "operationType" : NewBodyOperationType.REMOVE, "oppositeDirection" : true, "depth" : 4 * mm});
        }
        {
            var Q0;
            Q0=makeQuery(id+"F3.opExtrude","CAP_EDGE",EDGE,{"disambiguationData":[OSD([sQuery(id+"F2.wireOp",EDGE,"E4.right")])],"isStart":false});
            fillet(context, id + "F10", {"entities" : qUnion([Q0]), "radius" : 1.5 * mm, "tangentPropagation" : true, "allowEdgeOverflow" : false});
        }
    });
